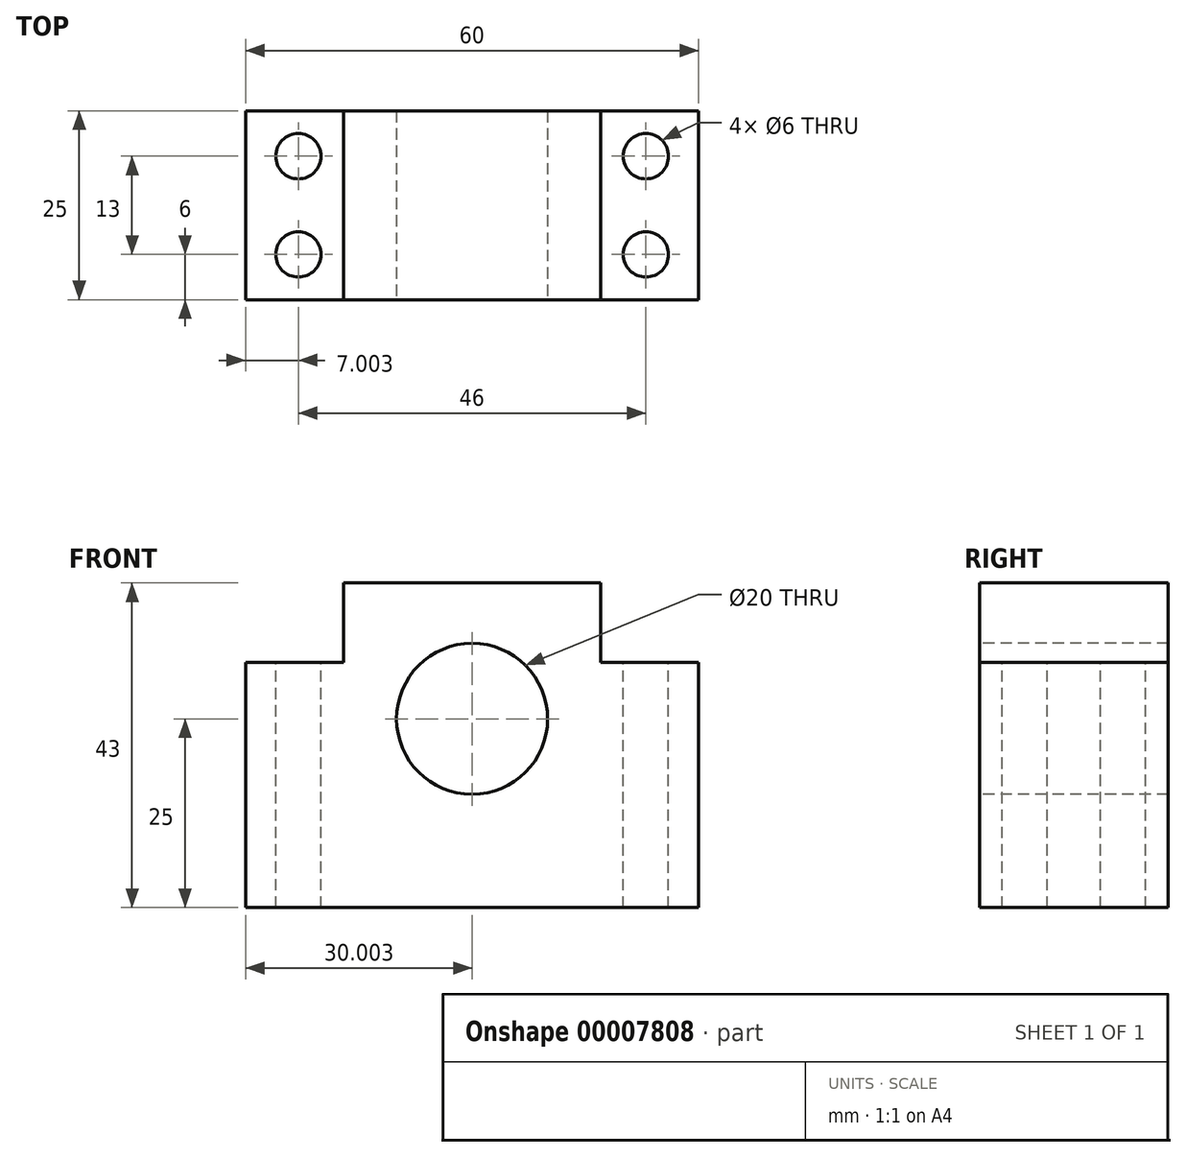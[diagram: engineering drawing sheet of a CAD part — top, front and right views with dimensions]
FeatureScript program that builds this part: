
annotation { "Feature Type Name" : "Feature", "Feature Type Description" : "" }
export const myFeature = defineFeature(function(context is Context, id is Id, definition is map)
    precondition{}
    {
        {
            var Q0;
            Q0=qCreatedBy(makeId("Front.planeOp"),FACE);
            var sketch = newSketch(context, id + "F0", { "sketchPlane" : qUnion([Q0])});
            skLineSegment(sketch, "E0.bottom", {"start": v(-29.66, 0) * mm, "end": v(30.34, 0) * mm});
            skLineSegment(sketch, "E0.top", {"start": v(-29.66, 32.5) * mm, "end": v(-16.66, 32.5) * mm});
            skLineSegment(sketch, "E0.left", {"start": v(-29.66, 0) * mm, "end": v(-29.66, 32.5) * mm});
            skLineSegment(sketch, "E0.right", {"start": v(30.34, 0) * mm, "end": v(30.34, 32.5) * mm});
            skLineSegment(sketch, "E1.top", {"start": v(-16.66, 43) * mm, "end": v(17.34, 43) * mm});
            skLineSegment(sketch, "E1.left", {"start": v(-16.66, 32.5) * mm, "end": v(-16.66, 43) * mm});
            skLineSegment(sketch, "E1.right", {"start": v(17.34, 32.5) * mm, "end": v(17.34, 43) * mm});
            skLineSegment(sketch, "E2.trimOffspring", {"start": v(17.34, 32.5) * mm, "end": v(30.34, 32.5) * mm});
            skSolve(sketch);
        }
        {
            var Q0;
            Q0 = qSketchRegion(id + "F0", true);
            extrude(context, id + "F1", {"entities" : qUnion([Q0]), "oppositeDirection" : true, "depth" : 25 * mm});
        }
        {
            var Q0;
            Q0=makeQuery(id+"F1.opExtrude","SWEPT_FACE",FACE,{"disambiguationData":[OSD([sQuery(id+"F0.wireOp",EDGE,"E2.trimOffspring")])]});
            var sketch = newSketch(context, id + "F2", { "sketchPlane" : qUnion([Q0])});
            skCircle(sketch, "E3", {"center": v(23.34, 19) * mm, "radius": 3 * mm});
            skCircle(sketch, "E4", {"center": v(23.34, 6) * mm, "radius": 3 * mm});
            skCircle(sketch, "E5.0.MirrorC", {"center": v(-22.66, 19) * mm, "radius": 3 * mm});
            skCircle(sketch, "E6.0.MirrorC", {"center": v(-22.66, 6) * mm, "radius": 3 * mm});
            skLineSegment(sketch, "E7", {"start": v(30.34, 0) * mm, "end": v(30.34, -7.45) * mm, "construction": true});
            skLineSegment(sketch, "E8.0", {"start": v(0.34, 0) * mm, "end": v(0.34, -7.45) * mm});
            skSolve(sketch);
        }
        {
            var Q0;
            Q0 = qSketchRegion(id + "F2", true);
            extrude(context, id + "F3", {"entities" : qUnion([Q0]), "operationType" : NewBodyOperationType.REMOVE, "endBound" : BoundingType.THROUGH_ALL, "oppositeDirection" : true, "depth" : 25 * mm});
        }
        {
            var Q0;
            Q0=makeQuery(id+"F1.opExtrude","CAP_FACE",FACE,{"disambiguationData":[OSD([sQuery(id+"F0.wireOp",EDGE,"E0.bottom"),sQuery(id+"F0.wireOp",EDGE,"E0.top"),sQuery(id+"F0.wireOp",EDGE,"E0.left"),sQuery(id+"F0.wireOp",EDGE,"E0.right"),sQuery(id+"F0.wireOp",EDGE,"E1.top"),sQuery(id+"F0.wireOp",EDGE,"E1.left"),sQuery(id+"F0.wireOp",EDGE,"E1.right"),sQuery(id+"F0.wireOp",EDGE,"E2.trimOffspring")])],"isStart":true});
            var sketch = newSketch(context, id + "F4", { "sketchPlane" : qUnion([Q0])});
            skCircle(sketch, "E9", {"center": v(0.34, 25) * mm, "radius": 10 * mm});
            skSolve(sketch);
        }
        {
            var Q0;
            Q0 = qSketchRegion(id + "F4", true);
            extrude(context, id + "F5", {"entities" : qUnion([Q0]), "operationType" : NewBodyOperationType.REMOVE, "endBound" : BoundingType.THROUGH_ALL, "oppositeDirection" : true, "depth" : 25 * mm});
        }
    });
